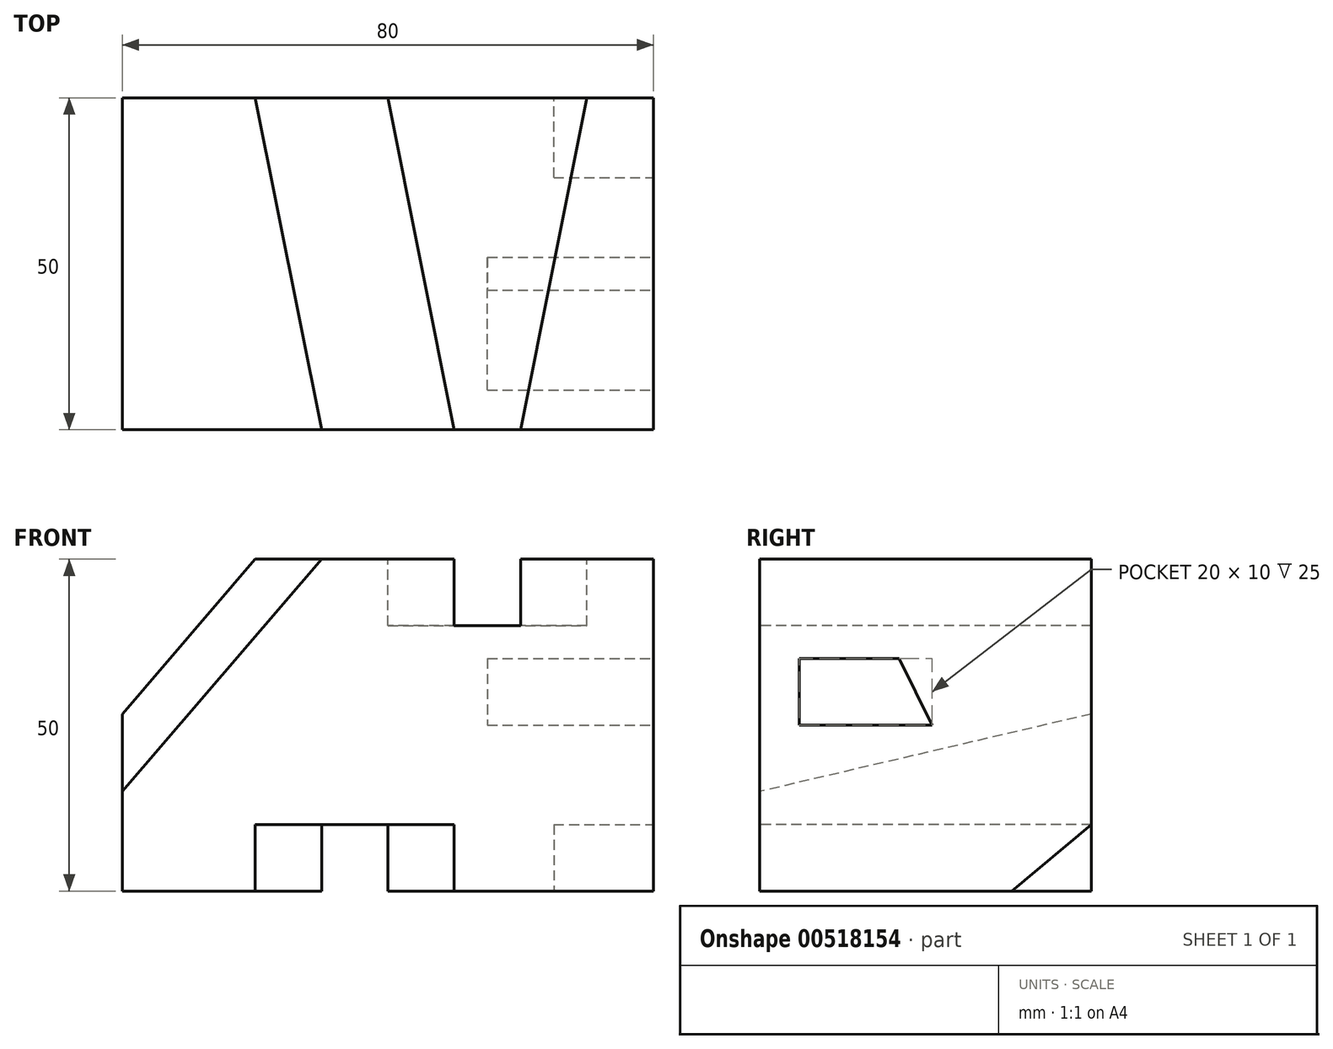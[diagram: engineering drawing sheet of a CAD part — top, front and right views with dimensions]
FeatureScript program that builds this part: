
annotation { "Feature Type Name" : "Feature", "Feature Type Description" : "" }
export const myFeature = defineFeature(function(context is Context, id is Id, definition is map)
    precondition{}
    {
        {
            var Q0;
            Q0=qCreatedBy(makeId("Top.planeOp"),FACE);
            var sketch = newSketch(context, id + "F0", { "sketchPlane" : qUnion([Q0])});
            skLineSegment(sketch, "E0.bottom", {"start": v(0, 0) * mm, "end": v(80, 0) * mm});
            skLineSegment(sketch, "E0.top", {"start": v(0, 50) * mm, "end": v(80, 50) * mm});
            skLineSegment(sketch, "E0.left", {"start": v(0, 0) * mm, "end": v(0, 50) * mm});
            skLineSegment(sketch, "E0.right", {"start": v(80, 0) * mm, "end": v(80, 50) * mm});
            skSolve(sketch);
        }
        {
            var Q0;
            Q0=makeQuery(id+"F0.imprint","IMPRINT",FACE,{"disambiguationData":[TD([[makeQuery(id+"F0.imprint","IMPRINT",EDGE,{"derivedFrom":sQuery(id+"F0.wireOp",EDGE,"E0.bottom")}),1.0]])]});
            extrude(context, id + "F1", {"entities" : qUnion([Q0]), "depth" : 50 * mm, "offsetDistance" : 25 * mm});
        }
        {
            var Q0;
            Q0=makeQuery(id+"F1.opExtrude","CAP_FACE",FACE,{"disambiguationData":[OSD([sQuery(id+"F0.wireOp",EDGE,"E0.bottom"),sQuery(id+"F0.wireOp",EDGE,"E0.top"),sQuery(id+"F0.wireOp",EDGE,"E0.left"),sQuery(id+"F0.wireOp",EDGE,"E0.right")])],"isStart":false});
            var sketch = newSketch(context, id + "F2", { "sketchPlane" : qUnion([Q0])});
            skLineSegment(sketch, "E1", {"start": v(70, 50) * mm, "end": v(60, 0) * mm});
            skLineSegment(sketch, "E2", {"start": v(50, 0) * mm, "end": v(40, 50) * mm});
            skSolve(sketch);
        }
        {
            var Q0;
            {var subQ0=sQuery(id+"F2.wireOp",EDGE,"E1");Q0=makeQuery(id+"F2.imprint","IMPRINT",FACE,{"disambiguationData":[TD([[makeQuery(id+"F2.imprint","IMPRINT",EDGE,{"derivedFrom":subQ0}),-1.0]])]});}
            extrude(context, id + "F3", {"entities" : qUnion([Q0]), "operationType" : NewBodyOperationType.REMOVE, "oppositeDirection" : true, "depth" : 10 * mm, "offsetDistance" : 25 * mm});
        }
        {
            var Q0;
            Q0=makeQuery(id+"F1.opExtrude","CAP_FACE",FACE,{"disambiguationData":[OSD([sQuery(id+"F0.wireOp",EDGE,"E0.bottom"),sQuery(id+"F0.wireOp",EDGE,"E0.top"),sQuery(id+"F0.wireOp",EDGE,"E0.left"),sQuery(id+"F0.wireOp",EDGE,"E0.right")])],"isStart":true});
            var sketch = newSketch(context, id + "F4", { "sketchPlane" : qUnion([Q0])});
            skLineSegment(sketch, "E3", {"start": v(40, -50) * mm, "end": v(50, 0) * mm});
            skLineSegment(sketch, "E4", {"start": v(20, 0) * mm, "end": v(30, -50) * mm});
            skSolve(sketch);
        }
        {
            var Q0;
            {var subQ0=sQuery(id+"F4.wireOp",EDGE,"E3");Q0=makeQuery(id+"F4.imprint","IMPRINT",FACE,{"disambiguationData":[TD([[makeQuery(id+"F4.imprint","IMPRINT",EDGE,{"derivedFrom":subQ0}),1.0]])]});}
            extrude(context, id + "F5", {"entities" : qUnion([Q0]), "operationType" : NewBodyOperationType.REMOVE, "oppositeDirection" : true, "depth" : 10 * mm, "offsetDistance" : 25 * mm});
        }
        {
            var Q0;
            Q0=makeQuery(id+"F1.opExtrude","SWEPT_FACE",FACE,{"disambiguationData":[OSD([sQuery(id+"F0.wireOp",EDGE,"E0.right")])]});
            var sketch = newSketch(context, id + "F6", { "sketchPlane" : qUnion([Q0])});
            skLineSegment(sketch, "E5.bottom", {"start": v(6, 35) * mm, "end": v(21, 35) * mm});
            skLineSegment(sketch, "E5.top", {"start": v(6, 25) * mm, "end": v(26, 25) * mm});
            skLineSegment(sketch, "E5.left", {"start": v(6, 35) * mm, "end": v(6, 25) * mm});
            skLineSegment(sketch, "E6", {"start": v(26, 25) * mm, "end": v(21, 35) * mm});
            skSolve(sketch);
        }
        {
            var Q0;
            Q0=makeQuery(id+"F6.imprint","IMPRINT",FACE,{"disambiguationData":[TD([[makeQuery(id+"F6.imprint","IMPRINT",EDGE,{"derivedFrom":sQuery(id+"F6.wireOp",EDGE,"E5.bottom")}),-1.0]])]});
            extrude(context, id + "F7", {"entities" : qUnion([Q0]), "operationType" : NewBodyOperationType.REMOVE, "oppositeDirection" : true, "depth" : 25 * mm, "offsetDistance" : 25 * mm});
        }
        {
            var Q0;
            Q0=makeQuery(id+"F1.opExtrude","SWEPT_FACE",FACE,{"disambiguationData":[OSD([sQuery(id+"F0.wireOp",EDGE,"E0.right")])]});
            var sketch = newSketch(context, id + "F8", { "sketchPlane" : qUnion([Q0])});
            skLineSegment(sketch, "E7", {"start": v(50, 10) * mm, "end": v(38, 0) * mm});
            skSolve(sketch);
        }
        {
            var Q0;
            {var subQ0=sQuery(id+"F8.wireOp",EDGE,"E7");Q0=makeQuery(id+"F8.imprint","IMPRINT",FACE,{"disambiguationData":[TD([[makeQuery(id+"F8.imprint","IMPRINT",EDGE,{"derivedFrom":subQ0}),1.0]])]});}
            extrude(context, id + "F9", {"entities" : qUnion([Q0]), "operationType" : NewBodyOperationType.REMOVE, "oppositeDirection" : true, "depth" : 15 * mm, "offsetDistance" : 25 * mm});
        }
        {
            var Q0;
            {var subQ0=sQuery(id+"F0.wireOp",EDGE,"E0.bottom");var subQ1=sQuery(id+"F0.wireOp",EDGE,"E0.top");var subQ2=sQuery(id+"F0.wireOp",EDGE,"E0.left");Q0=makeQuery(id+"F3.boolean.opBoolean","SPLIT",FACE,{"disambiguationData":[TD([makeQuery(id+"F1.opExtrude","SWEPT_FACE",FACE,{"disambiguationData":[OSD([subQ2])]})])],"derivedFrom":makeQuery(id+"F1.opExtrude","CAP_FACE",FACE,{"disambiguationData":[OSD([subQ0,subQ1,subQ2,sQuery(id+"F0.wireOp",EDGE,"E0.right")])],"isStart":false})});}
            var sketch = newSketch(context, id + "F10", { "sketchPlane" : qUnion([Q0])});
            skLineSegment(sketch, "E8", {"start": v(20, 50) * mm, "end": v(30, 0) * mm});
            skSolve(sketch);
        }
        {
            var Q0;
            Q0=makeQuery(id+"F1.opExtrude","SWEPT_FACE",FACE,{"disambiguationData":[OSD([sQuery(id+"F0.wireOp",EDGE,"E0.bottom")])]});
            var sketch = newSketch(context, id + "F11", { "sketchPlane" : qUnion([Q0])});
            skLineSegment(sketch, "E9", {"start": v(30, 50) * mm, "end": v(0, 15) * mm});
            skSolve(sketch);
        }
        {
            var Q0;
            {var subQ0=sQuery(id+"F10.wireOp",EDGE,"E8");Q0=makeQuery(id+"F10.imprint","IMPRINT",FACE,{"disambiguationData":[TD([[makeQuery(id+"F10.imprint","IMPRINT",EDGE,{"derivedFrom":subQ0}),-1.0]])]});}
            var Q1;
            Q1=sQuery(id+"F11.wireOp",EDGE,"E9");
            sweep(context, id + "F12", {"operationType" : NewBodyOperationType.REMOVE, "profiles" : qUnion([Q0]), "path" : qUnion([Q1])});
        }
    });
